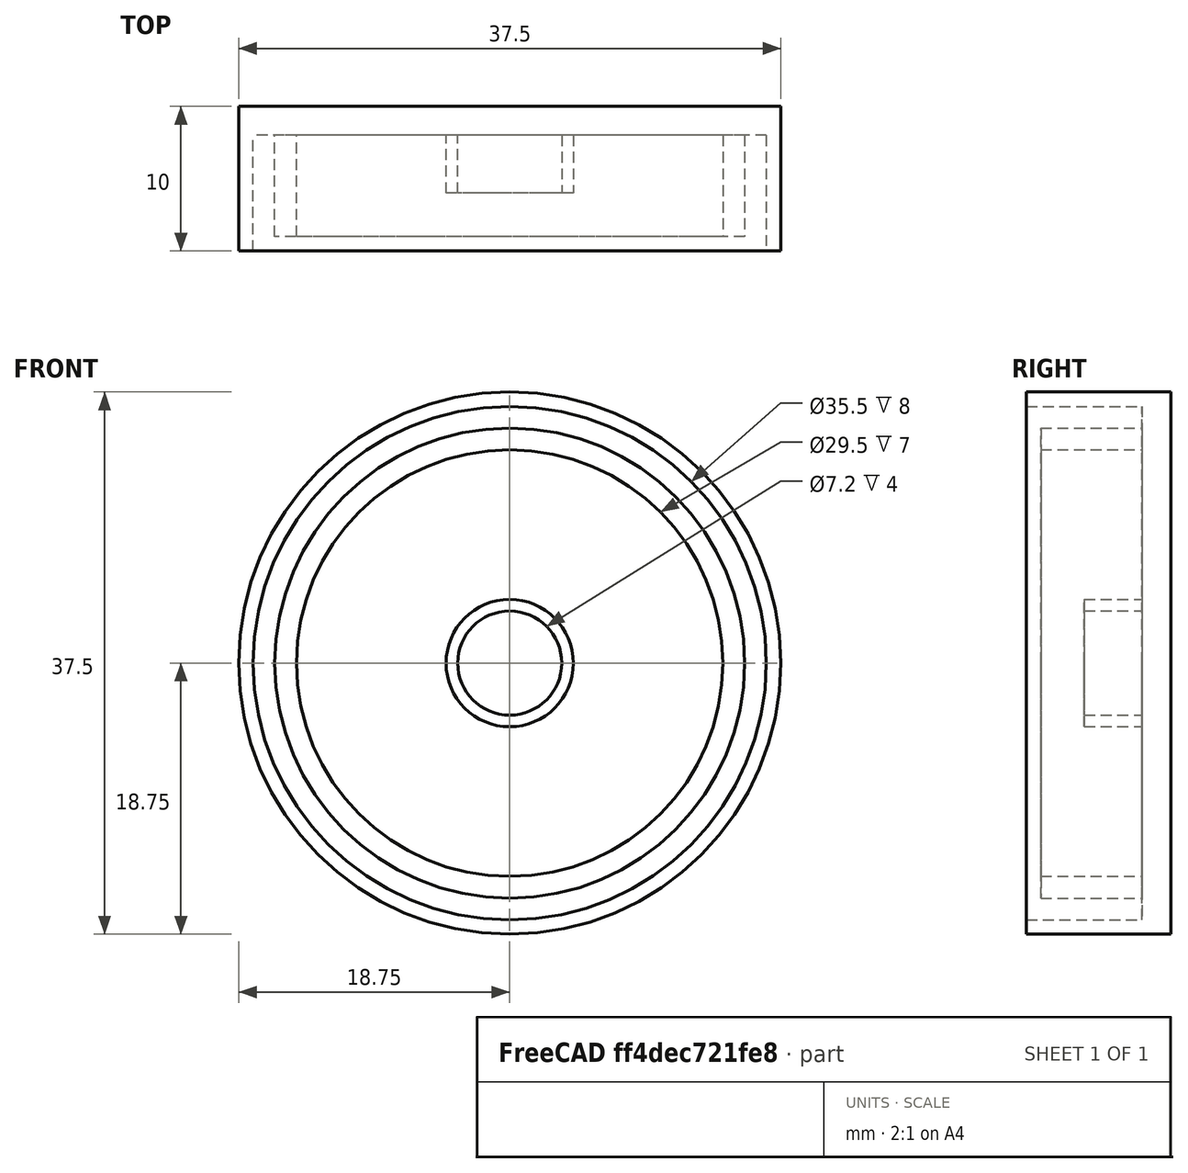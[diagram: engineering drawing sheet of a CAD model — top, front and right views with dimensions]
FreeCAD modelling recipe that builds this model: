
FCSTD DOCUMENT  (FreeCAD 0.14R2800 (Git))
Label: Button
License: CC-BY 3.0
LicenseURL: http://creativecommons.org/licenses/by/3.0/
objects: Sketcher::SketchObject×8, PartDesign::Pad×8, Part::MultiFuse×3, Part::Box×2, App::DocumentObjectGroup×2, Mesh::Feature×2, Part::Cut×1
note: 30 computed .brp shape members not serialized (recipe doc carries the construction recipe); baked Part::Feature solids carry a one-line shape summary decoded from their .brp

FEATURE [Sketcher::SketchObject] Sketch  label="ButtonBottomCap-Sketch"
  Placement = pos=(0,0,0) rot=(1,0,0;1.5708rad)
  sketch-geometry (1):
    g0: Circle CenterX=0 CenterY=0 CenterZ=0 NormalX=0 NormalY=0 NormalZ=1 Radius=17.5
  constraints (2):
    c: Radius(g0) = 17.5
    c: Coincident(g0,g-1)
FEATURE [Sketcher::SketchObject] Sketch001  label="ButtonBottomInner-Box"
  Placement = pos=(0,0,0) rot=(1,0,0;1.5708rad)
  sketch-geometry (12):
    g0: Circle [constr] CenterX=0 CenterY=0 CenterZ=0 NormalX=0 NormalY=0 NormalZ=1 Radius=17.5
    g1: Circle [constr] CenterX=0 CenterY=0 CenterZ=0 NormalX=0 NormalY=0 NormalZ=1 Radius=16.5
    g2: Circle [constr] CenterX=0 CenterY=0 CenterZ=0 NormalX=0 NormalY=0 NormalZ=1 Radius=14.5
    g3: Circle [constr] CenterX=0 CenterY=0 CenterZ=0 NormalX=0 NormalY=0 NormalZ=1 Radius=13.5
    g4: LineSegment StartX=-7 StartY=-7 StartZ=0 EndX=7 EndY=-7 EndZ=0
    g5: LineSegment StartX=7 StartY=-7 StartZ=0 EndX=7 EndY=7 EndZ=0
    g6: LineSegment StartX=7 StartY=7 StartZ=0 EndX=-7 EndY=7 EndZ=0
    g7: LineSegment StartX=-7 StartY=7 StartZ=0 EndX=-7 EndY=-7 EndZ=0
    g8: LineSegment StartX=-7.5 StartY=-7.5 StartZ=0 EndX=7.5 EndY=-7.5 EndZ=0
    g9: LineSegment StartX=7.5 StartY=-7.5 StartZ=0 EndX=7.5 EndY=7.5 EndZ=0
    g10: LineSegment StartX=7.5 StartY=7.5 StartZ=0 EndX=-7.5 EndY=7.5 EndZ=0
    g11: LineSegment StartX=-7.5 StartY=7.5 StartZ=0 EndX=-7.5 EndY=-7.5 EndZ=0
  constraints (32):
    c: Radius(g0) = 17.5
    c: Coincident(g0,g-1)
    c: Coincident(g1,g0)
    c: Radius(g1) = 16.5
    c: Radius(g2) = 14.5
    c: Coincident(g2,g-1)
    c: Radius(g3) = 13.5
    c: Coincident(g3,g-1)
    c: Coincident(g4,g5)
    c: Coincident(g5,g6)
    c: Coincident(g6,g7)
    c: Coincident(g7,g4)
    c: Horizontal(g4)
    c: Horizontal(g6)
    c: Vertical(g5)
    c: Vertical(g7)
    c: Equal(g5,g4)
    c: DistanceX(g4) = 7
    c: DistanceY(g4) = -7
    c: DistanceX(g6) = -14
    c: Coincident(g8,g9)
    c: Coincident(g9,g10)
    c: Coincident(g10,g11)
    c: Coincident(g11,g8)
    c: Horizontal(g8)
    c: Horizontal(g10)
    c: Vertical(g9)
    c: Vertical(g11)
    c: Equal(g11,g8)
    c: DistanceX(g8) = 15
    c: DistanceX(g8) = 7.5
    c: DistanceY(g8) = -7.5
FEATURE [Part::Box] Box  label="WireHoles"
  Height = 10
  Length = 1
  Placement = pos=(-7,-3,-5.5) rot=(0,0,1;0rad)
  Width = 10
FEATURE [Part::Box] Box001  label="WireHoles2"
  Height = 10
  Length = 1
  Placement = pos=(6,-3,-5.5) rot=(0,0,1;0rad)
  Width = 10
FEATURE [Part::MultiFuse] Fusion
  Shapes = -> [Box,Box001]
FEATURE [Sketcher::SketchObject] Sketch002  label="ButtonTopPad"
  Placement = pos=(0,7.8,0) rot=(-1,0,0;4.71239rad)
  sketch-geometry (1):
    g0: Circle CenterX=0 CenterY=0 CenterZ=0 NormalX=0 NormalY=0 NormalZ=1 Radius=18.75
  constraints (2):
    c: Coincident(g0,g-1)
    c: Radius(g0) = 18.75
FEATURE [PartDesign::Pad] Pad001  label="TopPad"
  Length = 2
  Length2 = 100
  Placement = pos=(0,7.8,0) rot=(-1,0,0;4.71239rad)
  Reversed = true
  Sketch = -> Sketch002
  Type = 0
FEATURE [Sketcher::SketchObject] Sketch003  label="TopStructure"
  Placement = pos=(0,7.8,0) rot=(-1,0,0;4.71239rad)
  sketch-geometry (6):
    g0: Circle [constr] CenterX=0 CenterY=0 CenterZ=0 NormalX=0 NormalY=0 NormalZ=1 Radius=17.75
    g1: Circle [constr] CenterX=0 CenterY=0 CenterZ=0 NormalX=0 NormalY=0 NormalZ=1 Radius=18.75
    g2: Circle CenterX=0 CenterY=0 CenterZ=0 NormalX=0 NormalY=0 NormalZ=1 Radius=3.6
    g3: Circle CenterX=0 CenterY=0 CenterZ=0 NormalX=0 NormalY=0 NormalZ=1 Radius=4.4
    g4: Circle [constr] CenterX=0 CenterY=0 CenterZ=0 NormalX=0 NormalY=0 NormalZ=1 Radius=16.25
    g5: Circle [constr] CenterX=0 CenterY=0 CenterZ=0 NormalX=0 NormalY=0 NormalZ=1 Radius=14.75
  constraints (12):
    c: Radius(g0) = 17.75
    c: Coincident(g0,g-1)
    c: Coincident(g0,g1)
    c: Radius(g1) = 18.75
    c: Radius(g2) = 3.6
    c: Coincident(g2,g1)
    c: Radius(g3) = 4.4
    c: Coincident(g3,g2)
    c: Radius(g4) = 16.25
    c: Coincident(g4,g-1)
    c: Radius(g5) = 14.75
    c: Coincident(g5,g-1)
FEATURE [PartDesign::Pad] Pad002  label="CenterShaft"
  Length = 4
  Length2 = 100
  Placement = pos=(0,7.8,0) rot=(-1,0,0;4.71239rad)
  Sketch = -> Sketch003
  Type = 0
FEATURE [Sketcher::SketchObject] Sketch003001  label="TopGuideRing"
  Placement = pos=(0,7.8,0) rot=(1,0,0;1.5708rad)
  sketch-geometry (6):
    g0: Circle [constr] CenterX=0 CenterY=0 CenterZ=0 NormalX=0 NormalY=0 NormalZ=1 Radius=17.75
    g1: Circle [constr] CenterX=0 CenterY=0 CenterZ=0 NormalX=0 NormalY=0 NormalZ=1 Radius=18.75
    g2: Circle [constr] CenterX=0 CenterY=0 CenterZ=0 NormalX=0 NormalY=0 NormalZ=1 Radius=3.375
    g3: Circle [constr] CenterX=0 CenterY=0 CenterZ=0 NormalX=0 NormalY=0 NormalZ=1 Radius=4.375
    g4: Circle CenterX=0 CenterY=0 CenterZ=0 NormalX=0 NormalY=0 NormalZ=1 Radius=16.25
    g5: Circle CenterX=0 CenterY=0 CenterZ=0 NormalX=0 NormalY=0 NormalZ=1 Radius=14.75
  constraints (12):
    c: Radius(g0) = 17.75
    c: Coincident(g0,g-1)
    c: Coincident(g0,g1)
    c: Radius(g1) = 18.75
    c: Radius(g2) = 3.375
    c: Coincident(g2,g1)
    c: Radius(g3) = 4.375
    c: Coincident(g3,g2)
    c: Radius(g4) = 16.25
    c: Coincident(g4,g-1)
    c: Radius(g5) = 14.75
    c: Coincident(g5,g-1)
FEATURE [Sketcher::SketchObject] Sketch003002  label="TopStructure002"
  Placement = pos=(0,7.8,0) rot=(1,0,0;1.5708rad)
  sketch-geometry (6):
    g0: Circle CenterX=0 CenterY=0 CenterZ=0 NormalX=0 NormalY=0 NormalZ=1 Radius=17.75
    g1: Circle CenterX=0 CenterY=0 CenterZ=0 NormalX=0 NormalY=0 NormalZ=1 Radius=18.75
    g2: Circle [constr] CenterX=0 CenterY=0 CenterZ=0 NormalX=0 NormalY=0 NormalZ=1 Radius=3.375
    g3: Circle [constr] CenterX=0 CenterY=0 CenterZ=0 NormalX=0 NormalY=0 NormalZ=1 Radius=4.375
    g4: Circle [constr] CenterX=0 CenterY=0 CenterZ=0 NormalX=0 NormalY=0 NormalZ=1 Radius=16.25
    g5: Circle [constr] CenterX=0 CenterY=0 CenterZ=0 NormalX=0 NormalY=0 NormalZ=1 Radius=14.75
  constraints (12):
    c: Radius(g0) = 17.75
    c: Coincident(g0,g-1)
    c: Coincident(g0,g1)
    c: Radius(g1) = 18.75
    c: Radius(g2) = 3.375
    c: Coincident(g2,g1)
    c: Radius(g3) = 4.375
    c: Coincident(g3,g2)
    c: Radius(g4) = 16.25
    c: Coincident(g4,g-1)
    c: Radius(g5) = 14.75
    c: Coincident(g5,g-1)
FEATURE [PartDesign::Pad] Pad003  label="TopGuideRing001"
  Length = 7
  Length2 = 100
  Placement = pos=(0,7.8,0) rot=(1,0,0;1.5708rad)
  Sketch = -> Sketch003001
  Type = 0
FEATURE [PartDesign::Pad] Pad004  label="TopOuter"
  Length = 8
  Length2 = 100
  Placement = pos=(0,7.8,0) rot=(1,0,0;1.5708rad)
  Sketch = -> Sketch003002
  Type = 0
FEATURE [Part::MultiFuse] Fusion001  label="TopFusion"
  Shapes = -> [Pad004,Pad001,Pad002,Pad003]
FEATURE [App::DocumentObjectGroup] Group002  label="Button Top"
  Group = -> [Pad001,Fusion001]
FEATURE [Sketcher::SketchObject] Sketch001001  label="BottomOuterRing"
  Placement = pos=(0,0,0) rot=(1,0,0;1.5708rad)
  sketch-geometry (12):
    g0: Circle CenterX=0 CenterY=0 CenterZ=0 NormalX=0 NormalY=0 NormalZ=1 Radius=17.5
    g1: Circle CenterX=0 CenterY=0 CenterZ=0 NormalX=0 NormalY=0 NormalZ=1 Radius=16.5
    g2: Circle [constr] CenterX=0 CenterY=0 CenterZ=0 NormalX=0 NormalY=0 NormalZ=1 Radius=14.5
    g3: Circle [constr] CenterX=0 CenterY=0 CenterZ=0 NormalX=0 NormalY=0 NormalZ=1 Radius=13.5
    g4: LineSegment [constr] StartX=-7 StartY=-7 StartZ=0 EndX=7 EndY=-7 EndZ=0
    g5: LineSegment [constr] StartX=7 StartY=-7 StartZ=0 EndX=7 EndY=7 EndZ=0
    g6: LineSegment [constr] StartX=7 StartY=7 StartZ=0 EndX=-7 EndY=7 EndZ=0
    g7: LineSegment [constr] StartX=-7 StartY=7 StartZ=0 EndX=-7 EndY=-7 EndZ=0
    g8: LineSegment [constr] StartX=-7.5 StartY=-7.5 StartZ=0 EndX=7.5 EndY=-7.5 EndZ=0
    g9: LineSegment [constr] StartX=7.5 StartY=-7.5 StartZ=0 EndX=7.5 EndY=7.5 EndZ=0
    g10: LineSegment [constr] StartX=7.5 StartY=7.5 StartZ=0 EndX=-7.5 EndY=7.5 EndZ=0
    g11: LineSegment [constr] StartX=-7.5 StartY=7.5 StartZ=0 EndX=-7.5 EndY=-7.5 EndZ=0
  constraints (32):
    c: Radius(g0) = 17.5
    c: Coincident(g0,g-1)
    c: Coincident(g1,g0)
    c: Radius(g1) = 16.5
    c: Radius(g2) = 14.5
    c: Coincident(g2,g-1)
    c: Radius(g3) = 13.5
    c: Coincident(g3,g-1)
    c: Coincident(g4,g5)
    c: Coincident(g5,g6)
    c: Coincident(g6,g7)
    c: Coincident(g7,g4)
    c: Horizontal(g4)
    c: Horizontal(g6)
    c: Vertical(g5)
    c: Vertical(g7)
    c: Equal(g5,g4)
    c: DistanceX(g4) = 7
    c: DistanceY(g4) = -7
    c: DistanceX(g6) = -14
    c: Coincident(g8,g9)
    c: Coincident(g9,g10)
    c: Coincident(g10,g11)
    c: Coincident(g11,g8)
    c: Horizontal(g8)
    c: Horizontal(g10)
    c: Vertical(g9)
    c: Vertical(g11)
    c: Equal(g11,g8)
    c: DistanceX(g8) = 15
    c: DistanceX(g8) = 7.5
    c: DistanceY(g8) = -7.5
FEATURE [Sketcher::SketchObject] Sketch001001001  label="BottomInnerCircle"
  Placement = pos=(0,0,0) rot=(1,0,0;1.5708rad)
  sketch-geometry (12):
    g0: Circle [constr] CenterX=0 CenterY=0 CenterZ=0 NormalX=0 NormalY=0 NormalZ=1 Radius=17.5
    g1: Circle [constr] CenterX=0 CenterY=0 CenterZ=0 NormalX=0 NormalY=0 NormalZ=1 Radius=16.5
    g2: Circle CenterX=0 CenterY=0 CenterZ=0 NormalX=0 NormalY=0 NormalZ=1 Radius=14.5
    g3: Circle CenterX=0 CenterY=0 CenterZ=0 NormalX=0 NormalY=0 NormalZ=1 Radius=13.5
    g4: LineSegment [constr] StartX=-7 StartY=-7 StartZ=0 EndX=7 EndY=-7 EndZ=0
    g5: LineSegment [constr] StartX=7 StartY=-7 StartZ=0 EndX=7 EndY=7 EndZ=0
    g6: LineSegment [constr] StartX=7 StartY=7 StartZ=0 EndX=-7 EndY=7 EndZ=0
    g7: LineSegment [constr] StartX=-7 StartY=7 StartZ=0 EndX=-7 EndY=-7 EndZ=0
    g8: LineSegment [constr] StartX=-7.5 StartY=-7.5 StartZ=0 EndX=7.5 EndY=-7.5 EndZ=0
    g9: LineSegment [constr] StartX=7.5 StartY=-7.5 StartZ=0 EndX=7.5 EndY=7.5 EndZ=0
    g10: LineSegment [constr] StartX=7.5 StartY=7.5 StartZ=0 EndX=-7.5 EndY=7.5 EndZ=0
    g11: LineSegment [constr] StartX=-7.5 StartY=7.5 StartZ=0 EndX=-7.5 EndY=-7.5 EndZ=0
  constraints (32):
    c: Radius(g0) = 17.5
    c: Coincident(g0,g-1)
    c: Coincident(g1,g0)
    c: Radius(g1) = 16.5
    c: Radius(g2) = 14.5
    c: Coincident(g2,g-1)
    c: Radius(g3) = 13.5
    c: Coincident(g3,g-1)
    c: Coincident(g4,g5)
    c: Coincident(g5,g6)
    c: Coincident(g6,g7)
    c: Coincident(g7,g4)
    c: Horizontal(g4)
    c: Horizontal(g6)
    c: Vertical(g5)
    c: Vertical(g7)
    c: Equal(g5,g4)
    c: DistanceX(g4) = 7
    c: DistanceY(g4) = -7
    c: DistanceX(g6) = -14
    c: Coincident(g8,g9)
    c: Coincident(g9,g10)
    c: Coincident(g10,g11)
    c: Coincident(g11,g8)
    c: Horizontal(g8)
    c: Horizontal(g10)
    c: Vertical(g9)
    c: Vertical(g11)
    c: Equal(g11,g8)
    c: DistanceX(g8) = 15
    c: DistanceX(g8) = 7.5
    c: DistanceY(g8) = -7.5
FEATURE [PartDesign::Pad] Pad005  label="ButtonBox"
  Length = 4
  Length2 = 100
  Placement = pos=(0,0,0) rot=(1,0,0;1.5708rad)
  Sketch = -> Sketch001
  Type = 0
FEATURE [PartDesign::Pad] Pad006  label="InnerRing"
  Length = 4
  Length2 = 100
  Placement = pos=(0,0,0) rot=(1,0,0;1.5708rad)
  Sketch = -> Sketch001001001
  Type = 0
FEATURE [PartDesign::Pad] Pad007  label="BotOuterRing"
  Length = 4
  Length2 = 100
  Placement = pos=(0,0,0) rot=(1,0,0;1.5708rad)
  Sketch = -> Sketch001001
  Type = 0
FEATURE [PartDesign::Pad] Pad  label="BottomPad"
  Length = 1.5
  Length2 = 100
  Placement = pos=(0,0,0) rot=(1,0,0;1.5708rad)
  Reversed = true
  Sketch = -> Sketch
  Type = 0
FEATURE [Part::Cut] Cut  label="BottomPadW/Holes"
  Base = -> Pad
  Tool = -> Fusion
FEATURE [Part::MultiFuse] Fusion002  label="BottomFusion"
  Shapes = -> [Pad005,Pad006,Pad007,Cut]
FEATURE [App::DocumentObjectGroup] Group001  label="ButtonBottom"
  Group = -> [Pad005,Pad006,Pad007,Pad,Fusion,Cut,Fusion002]
FEATURE [Mesh::Feature] Mesh001  label="BottomFusion (Meshed)"
FEATURE [Mesh::Feature] Mesh  label="TopFusion (Meshed)"
